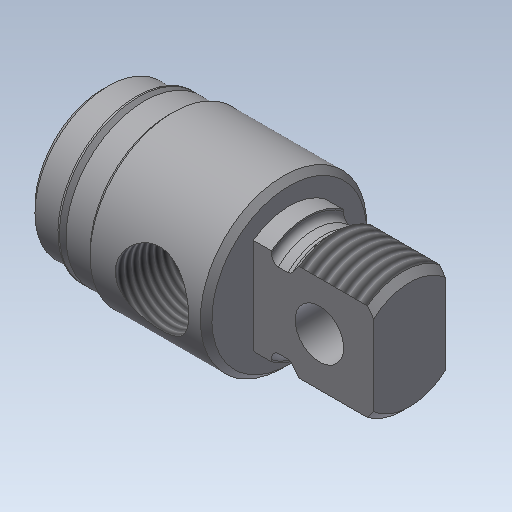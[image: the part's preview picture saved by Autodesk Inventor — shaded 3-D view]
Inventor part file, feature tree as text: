
AUTODESK INVENTOR PART (.ipt)
format: ipt  version: 2020 (Build 240168000, 168)  size: 351,744 bytes
history: native  units: in
note: dims shown in document units (in); Inventor stores cm internally (conversion verified against a paired STEP export)
features: other x154, sketch x7, revolve x4, thread x2, extrude x2, hole x1
ambient origin geometry x8: Origin, YZ Plane, XZ Plane, XY Plane, X Axis, Y Axis, Z Axis, Center Point
bodies: Solid1 (feature_tree)
feature tree (170):
  revolve  "Revolution1"  Angle=360.0deg
  revolve  "Revolution2"  [1 undecoded]
  thread  "Thread1"  [1 undecoded]
  extrude  "Extrusion1"  TaperAngle=360.0deg  [1 undecoded]
  hole  "Hole1"  [1 undecoded]
  revolve  "Revolution3"  [1 undecoded]
  thread  "Thread2"  [1 undecoded]
  revolve  "Revolution4"  [1 undecoded]
  extrude  "Extrusion2"  [1 undecoded]
  other  "1_XY"
  other  "1_YZ"
  other  "1_ZX"
  other  "1_X"
  other  "1_Y"
  other  "1_Z"
  other  "1_Center"
  other  "c1_XY"
  other  "c1_YZ"
  other  "c1_ZX"
  other  "c1_X"
  other  "c1_Y"
  other  "c1_Z"
  other  "c1_Center"
  other  "c2_XY"
  other  "c2_YZ"
  other  "c2_ZX"
  other  "c2_X"
  other  "c2_Y"
  other  "c2_Z"
  other  "c2_Center"
  other  "cc1_XY"
  other  "cc1_YZ"
  other  "cc1_ZX"
  other  "cc1_X"
  other  "cc1_Y"
  other  "cc1_Z"
  other  "cc1_Center"
  other  "cc2_XY"
  other  "cc2_YZ"
  other  "cc2_ZX"
  other  "cc2_X"
  other  "cc2_Y"
  other  "cc2_Z"
  other  "cc2_Center"
  other  "lovra1_XY"
  other  "lovra1_YZ"
  other  "lovra1_ZX"
  other  "lovra1_X"
  other  "lovra1_Y"
  other  "lovra1_Z"
  other  "lovra1_Center"
  other  "lovra2_XY"
  other  "lovra2_YZ"
  other  "lovra2_ZX"
  other  "lovra2_X"
  other  "lovra2_Y"
  other  "lovra2_Z"
  other  "lovra2_Center"
  other  "lovra21_XY"
  other  "lovra21_YZ"
  other  "lovra21_ZX"
  other  "lovra21_X"
  other  "lovra21_Y"
  other  "lovra21_Z"
  other  "lovra21_Center"
  other  "lovra22_XY"
  other  "lovra22_YZ"
  other  "lovra22_ZX"
  other  "lovra22_X"
  other  "lovra22_Y"
  other  "lovra22_Z"
  other  "lovra22_Center"
  other  "lovra3_XY"
  other  "lovra3_YZ"
  other  "lovra3_ZX"
  other  "lovra3_X"
  other  "lovra3_Y"
  other  "lovra3_Z"
  other  "lovra3_Center"
  other  "olen_XY"
  other  "olen_YZ"
  other  "olen_ZX"
  other  "olen_X"
  other  "olen_Y"
  other  "olen_Z"
  other  "olen_Center"
  other  "p1_XY"
  other  "p1_YZ"
  other  "p1_ZX"
  other  "p1_X"
  other  "p1_Y"
  other  "p1_Z"
  other  "p1_Center"
  other  "p2_XY"
  other  "p2_YZ"
  other  "p2_ZX"
  other  "p2_X"
  other  "p2_Y"
  other  "p2_Z"
  other  "p2_Center"
  other  "port_XY"
  other  "port_YZ"
  other  "port_ZX"
  other  "port_X"
  other  "port_Y"
  other  "port_Z"
  other  "port_Center"
  other  "port2_XY"
  other  "port2_YZ"
  other  "port2_ZX"
  other  "port2_X"
  other  "port2_Y"
  other  "port2_Z"
  other  "port2_Center"
  other  "thd1_XY"
  other  "thd1_YZ"
  other  "thd1_ZX"
  other  "thd1_X"
  other  "thd1_Y"
  other  "thd1_Z"
  other  "thd1_Center"
  other  "thd2_XY"
  other  "thd2_YZ"
  other  "thd2_ZX"
  other  "thd2_X"
  other  "thd2_Y"
  other  "thd2_Z"
  other  "thd2_Center"
  other  "to_mounting_bracket_XY"
  other  "to_mounting_bracket_YZ"
  other  "to_mounting_bracket_ZX"
  other  "to_mounting_bracket_X"
  other  "to_mounting_bracket_Y"
  other  "to_mounting_bracket_Z"
  other  "to_mounting_bracket_Center"
  other  "to_nut_XY"
  other  "to_nut_YZ"
  other  "to_nut_ZX"
  other  "to_nut_X"
  other  "to_nut_Y"
  other  "to_nut_Z"
  other  "to_nut_Center"
  other  "to_pin_XY"
  other  "to_pin_YZ"
  other  "to_pin_ZX"
  other  "to_pin_X"
  other  "to_pin_Y"
  other  "to_pin_Z"
  other  "to_pin_Center"
  other  "to_screw_XY"
  other  "to_screw_YZ"
  other  "to_screw_ZX"
  other  "to_screw_X"
  other  "to_screw_Y"
  other  "to_screw_Z"
  other  "to_screw_Center"
  other  "to_tube_XY"
  other  "to_tube_YZ"
  other  "to_tube_ZX"
  other  "to_tube_X"
  other  "to_tube_Y"
  other  "to_tube_Z"
  other  "to_tube_Center"
  sketch  "Sketch_8"  dims[d2=0.3547in d3=0.0in d4=0.625in d5=0.0in]
  sketch  "Sketch_15"  dims[d14=0.3021in d15=0.0in d16=360.0deg]
  sketch  "Sketch_9"  dims[d6=0.312in d7=0.75in d8=0.375in d9=0.25in d10=0.5635in d11=0.9284in d12=120.0deg d13=360.0deg]
  sketch  "Sketch4"  dims[d0=360.0deg d1=360.0deg]
  sketch  "Sketch_68"
  sketch  "Sketch_24"  dims[d17=0.5587in d18=0.0in]
  sketch  "Sketch_43"  dims[d19=0.0in d20=0.0in d21=0.0in d22=0.0in d23=0.0in d24=0.0in d25=0.0in d26=0.0in]
note: 8 required parameter values undecoded (feature->parameter linkage not recoverable at this tier; creation-order binding heuristic only, values carry confidence <= 0.55)